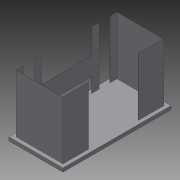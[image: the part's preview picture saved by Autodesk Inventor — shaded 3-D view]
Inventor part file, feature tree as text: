
AUTODESK INVENTOR PART (.ipt)
format: ipt  version: 2015 SP1 (Build 190203100, 203)  size: 149,504 bytes
history: native  units: in
note: dims shown in document units (in); Inventor stores cm internally (conversion verified against a paired STEP export)
features: extrude x6, sketch x6
ambient origin geometry x8: Origin, YZ Plane, XZ Plane, XY Plane, X Axis, Y Axis, Z Axis, Center Point
bodies: Solid1 (feature_tree)
feature tree (12):
  extrude  "Extrusion1"  Depth=15.0in
  extrude  "Extrusion2"  Depth=0.5in
  extrude  "Extrusion3"  Depth=8.0in TaperAngle=0.0deg
  extrude  "Extrusion4"  Depth=3.5in
  extrude  "Extrusion5"  Depth=2.0in
  extrude  "Extrusion6"  Depth=2.0in TaperAngle=0.0deg
  sketch  "Sketch1"  dims[d0=7.5in d1=15.0in]
  sketch  "Sketch2"  dims[d2=0.5in d3=0.0in d4=0.5in]
  sketch  "Sketch3"  dims[d5=0.0312in d6=8.0in d7=0.0in]
  sketch  "Sketch4"  dims[d9=3.5in d10=3.5in]
  sketch  "Sketch5"  dims[d11=2.0in d12=0.0in d13=2.0in]
  sketch  "Sketch6"  dims[d14=3.5in d15=2.0in d16=0.0in d17=3.5312in d18=1.0in d19=1.0in d20=1.0in d21=0.0in d22=1.0in d23=1.0in d24=1.0in d25=0.0in]
